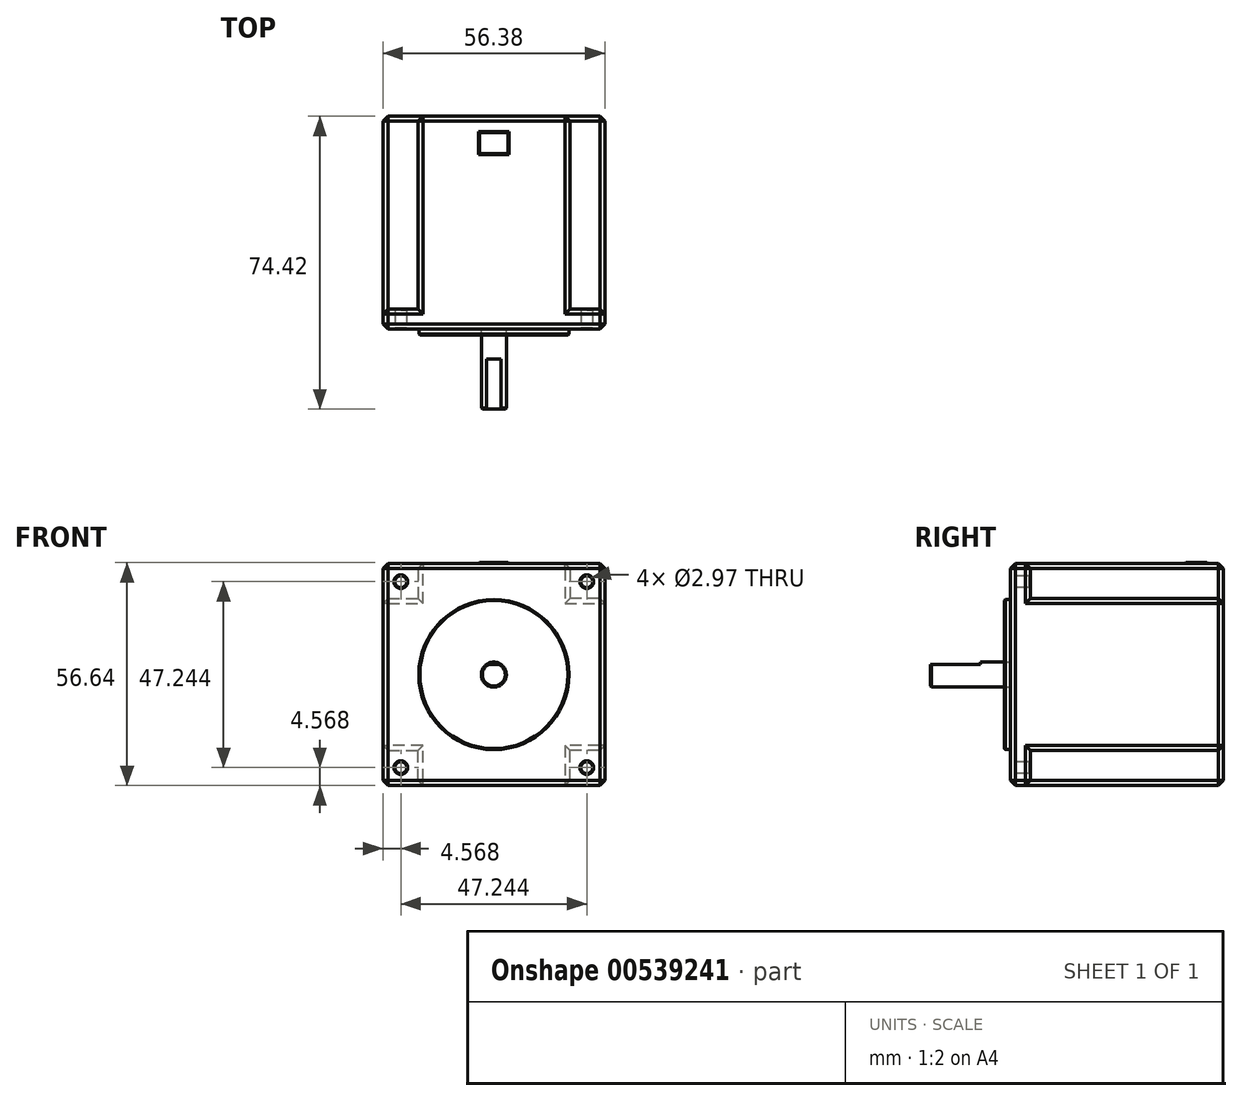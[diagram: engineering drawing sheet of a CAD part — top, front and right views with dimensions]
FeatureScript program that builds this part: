
annotation { "Feature Type Name" : "Feature", "Feature Type Description" : "" }
export const myFeature = defineFeature(function(context is Context, id is Id, definition is map)
    precondition{}
    {
        {
            var Q0;
            Q0=qCreatedBy(makeId("Front.planeOp"),FACE);
            var sketch = newSketch(context, id + "F0", { "sketchPlane" : qUnion([Q0])});
            skCircle(sketch, "E0", {"center": v(0, 0) * mm, "radius": 19.05 * mm});
            skLineSegment(sketch, "E1.bottom", {"start": v(28.2, 28.2) * mm, "end": v(-28.2, 28.2) * mm});
            skLineSegment(sketch, "E1.top", {"start": v(28.2, -28.2) * mm, "end": v(-28.2, -28.2) * mm});
            skLineSegment(sketch, "E1.left", {"start": v(28.2, 28.2) * mm, "end": v(28.2, -28.2) * mm});
            skLineSegment(sketch, "E1.right", {"start": v(-28.2, 28.2) * mm, "end": v(-28.2, -28.2) * mm});
            skCircle(sketch, "E2", {"center": v(0, 0) * mm, "radius": 3.18 * mm});
            skCircle(sketch, "E3", {"center": v(-23.62, 23.62) * mm, "radius": 1.49 * mm});
            skCircle(sketch, "E4", {"center": v(23.62, 23.62) * mm, "radius": 1.49 * mm});
            skCircle(sketch, "E5", {"center": v(23.62, -23.62) * mm, "radius": 1.49 * mm});
            skCircle(sketch, "E6", {"center": v(-23.62, -23.62) * mm, "radius": 1.49 * mm});
            skLineSegment(sketch, "E7", {"start": v(-23.62, 23.62) * mm, "end": v(-23.62, 28.2) * mm, "construction": true});
            skLineSegment(sketch, "E8", {"start": v(-23.62, 28.2) * mm, "end": v(-23.62, 23.62) * mm, "construction": true});
            skLineSegment(sketch, "E9", {"start": v(-23.62, 23.62) * mm, "end": v(-28.2, 23.62) * mm, "construction": true});
            skLineSegment(sketch, "E10", {"start": v(23.62, 23.62) * mm, "end": v(23.62, 28.2) * mm, "construction": true});
            skLineSegment(sketch, "E11", {"start": v(23.62, 23.62) * mm, "end": v(28.2, 23.62) * mm, "construction": true});
            skLineSegment(sketch, "E12", {"start": v(23.62, -23.62) * mm, "end": v(28.2, -23.62) * mm, "construction": true});
            skLineSegment(sketch, "E13", {"start": v(23.62, -23.62) * mm, "end": v(23.62, -28.2) * mm, "construction": true});
            skLineSegment(sketch, "E14", {"start": v(-23.62, -23.62) * mm, "end": v(-23.62, -28.2) * mm, "construction": true});
            skLineSegment(sketch, "E15", {"start": v(-23.62, -23.62) * mm, "end": v(-28.2, -23.62) * mm, "construction": true});
            skSolve(sketch);
        }
        {
            var Q0;
            Q0=qSketchRegion(id+"F0",true);
            var Q1;
            Q1=makeQuery(id+"F0.imprint","IMPRINT",FACE,{"disambiguationData":[TD([[makeQuery(id+"F0.imprint","IMPRINT",EDGE,{"derivedFrom":sQuery(id+"F0.wireOp",EDGE,"E0")}),1.0]])]});
            var Q2;
            Q2=makeQuery(id+"F0.imprint","IMPRINT",FACE,{"disambiguationData":[TD([[makeQuery(id+"F0.imprint","IMPRINT",EDGE,{"derivedFrom":sQuery(id+"F0.wireOp",EDGE,"E2")}),1.0]])]});
            extrude(context, id + "F1", {"entities" : qUnion([Q0, Q1, Q2]), "oppositeDirection" : true, "depth" : 54.1 * mm});
        }
        {
            var Q0;
            Q0=makeQuery(id+"F0.imprint","IMPRINT",FACE,{"disambiguationData":[TD([[makeQuery(id+"F0.imprint","IMPRINT",EDGE,{"derivedFrom":sQuery(id+"F0.wireOp",EDGE,"E0")}),1.0]])]});
            extrude(context, id + "F2", {"entities" : qUnion([Q0]), "operationType" : NewBodyOperationType.ADD, "depth" : 1.52 * mm});
        }
        {
            var Q0;
            Q0=makeQuery(id+"F0.imprint","IMPRINT",FACE,{"disambiguationData":[TD([[makeQuery(id+"F0.imprint","IMPRINT",EDGE,{"derivedFrom":sQuery(id+"F0.wireOp",EDGE,"E2")}),1.0]])]});
            extrude(context, id + "F3", {"entities" : qUnion([Q0]), "depth" : 20.32 * mm});
        }
        {
            var Q0;
            Q0=makeQuery(id+"F3.opExtrude","CAP_FACE",FACE,{"disambiguationData":[OSD([sQuery(id+"F0.wireOp",EDGE,"E2")])],"isStart":false});
            var sketch = newSketch(context, id + "F4", { "sketchPlane" : qUnion([Q0])});
            skLineSegment(sketch, "E16", {"start": v(-1.8, 2.62) * mm, "end": v(1.8, 2.62) * mm});
            skSolve(sketch);
        }
        {
            var Q0;
            {var subQ0=sQuery(id+"F4.wireOp",EDGE,"E16");Q0=makeQuery(id+"F4.imprint","IMPRINT",FACE,{"disambiguationData":[TD([[makeQuery(id+"F4.imprint","IMPRINT",EDGE,{"derivedFrom":subQ0}),1.0]])]});}
            extrude(context, id + "F5", {"entities" : qUnion([Q0]), "operationType" : NewBodyOperationType.REMOVE, "oppositeDirection" : true, "depth" : 12.7 * mm});
        }
        {
            var Q0;
            Q0=makeQuery(id+"F1.opExtrude","CAP_FACE",FACE,{"disambiguationData":[OSD([sQuery(id+"F0.wireOp",EDGE,"E1.bottom"),sQuery(id+"F0.wireOp",EDGE,"E1.top"),sQuery(id+"F0.wireOp",EDGE,"E1.left"),sQuery(id+"F0.wireOp",EDGE,"E1.right"),sQuery(id+"F0.wireOp",EDGE,"E3"),sQuery(id+"F0.wireOp",EDGE,"E4"),sQuery(id+"F0.wireOp",EDGE,"E5"),sQuery(id+"F0.wireOp",EDGE,"E6")])],"isStart":false});
            var sketch = newSketch(context, id + "F6", { "sketchPlane" : qUnion([Q0])});
            skLineSegment(sketch, "E17.bottom", {"start": v(-28.2, 28.2) * mm, "end": v(-19.3, 28.2) * mm});
            skLineSegment(sketch, "E17.top", {"start": v(-28.2, 19.3) * mm, "end": v(-19.3, 19.3) * mm});
            skLineSegment(sketch, "E17.left", {"start": v(-28.2, 28.2) * mm, "end": v(-28.2, 19.3) * mm});
            skLineSegment(sketch, "E17.right", {"start": v(-19.3, 28.2) * mm, "end": v(-19.3, 19.3) * mm});
            skLineSegment(sketch, "E18.bottom", {"start": v(28.2, 28.2) * mm, "end": v(19.3, 28.2) * mm});
            skLineSegment(sketch, "E18.top", {"start": v(28.2, 19.3) * mm, "end": v(19.3, 19.3) * mm});
            skLineSegment(sketch, "E18.left", {"start": v(28.2, 28.2) * mm, "end": v(28.2, 19.3) * mm});
            skLineSegment(sketch, "E18.right", {"start": v(19.3, 28.2) * mm, "end": v(19.3, 19.3) * mm});
            skLineSegment(sketch, "E19.bottom", {"start": v(28.2, -28.2) * mm, "end": v(19.3, -28.2) * mm});
            skLineSegment(sketch, "E19.top", {"start": v(28.2, -19.3) * mm, "end": v(19.3, -19.3) * mm});
            skLineSegment(sketch, "E19.left", {"start": v(28.2, -28.2) * mm, "end": v(28.2, -19.3) * mm});
            skLineSegment(sketch, "E19.right", {"start": v(19.3, -28.2) * mm, "end": v(19.3, -19.3) * mm});
            skLineSegment(sketch, "E20.bottom", {"start": v(-28.2, -28.2) * mm, "end": v(-19.3, -28.2) * mm});
            skLineSegment(sketch, "E20.top", {"start": v(-28.2, -19.3) * mm, "end": v(-19.3, -19.3) * mm});
            skLineSegment(sketch, "E20.left", {"start": v(-28.2, -28.2) * mm, "end": v(-28.2, -19.3) * mm});
            skLineSegment(sketch, "E20.right", {"start": v(-19.3, -28.2) * mm, "end": v(-19.3, -19.3) * mm});
            skSolve(sketch);
        }
        {
            var Q0;
            Q0=qSketchRegion(id+"F6",true);
            var Q1;
            {var subQ0=sQuery(id+"F0.wireOp",EDGE,"E1.right");var subQ1=sQuery(id+"F0.wireOp",EDGE,"E1.left");var subQ2=sQuery(id+"F0.wireOp",EDGE,"E1.top");var subQ3=sQuery(id+"F0.wireOp",EDGE,"E1.bottom");var subQ4=sQuery(id+"F0.wireOp",EDGE,"E3");var subQ5=sQuery(id+"F0.wireOp",EDGE,"E4");var subQ6=sQuery(id+"F0.wireOp",EDGE,"E5");var subQ7=sQuery(id+"F0.wireOp",EDGE,"E6");Q1=makeQuery(id+"F2.boolean.opBoolean","SPLIT",FACE,{"disambiguationData":[TD([makeQuery(id+"F1.opExtrude","SWEPT_FACE",FACE,{"disambiguationData":[OSD([subQ3])]})])],"derivedFrom":makeQuery(id+"F1.opExtrude","CAP_FACE",FACE,{"disambiguationData":[OSD([subQ3,subQ2,subQ1,subQ0,subQ4,subQ5,subQ6,subQ7])],"isStart":true})});}
            extrude(context, id + "F7", {"entities" : qUnion([Q0]), "operationType" : NewBodyOperationType.REMOVE, "oppositeDirection" : true, "endBoundEntityFace" : qUnion([Q1]), "depth" : 49.02 * mm});
        }
        {
            var Q0;
            Q0=makeQuery(id+"F1.opExtrude","SWEPT_FACE",FACE,{"disambiguationData":[OSD([sQuery(id+"F0.wireOp",EDGE,"E1.right")])]});
            var Q1;
            Q1=makeQuery(id+"F1.opExtrude","SWEPT_FACE",FACE,{"disambiguationData":[OSD([sQuery(id+"F0.wireOp",EDGE,"E1.bottom")])]});
            var Q2;
            Q2=makeQuery(id+"F1.opExtrude","SWEPT_FACE",FACE,{"disambiguationData":[OSD([sQuery(id+"F0.wireOp",EDGE,"E1.left")])]});
            var Q3;
            Q3=makeQuery(id+"F1.opExtrude","SWEPT_FACE",FACE,{"disambiguationData":[OSD([sQuery(id+"F0.wireOp",EDGE,"E1.top")])]});
            var Q4;
            Q4=makeQuery(id+"F1.opExtrude","CAP_FACE",FACE,{"disambiguationData":[OSD([sQuery(id+"F0.wireOp",EDGE,"E1.bottom"),sQuery(id+"F0.wireOp",EDGE,"E1.top"),sQuery(id+"F0.wireOp",EDGE,"E1.left"),sQuery(id+"F0.wireOp",EDGE,"E1.right"),sQuery(id+"F0.wireOp",EDGE,"E3"),sQuery(id+"F0.wireOp",EDGE,"E4"),sQuery(id+"F0.wireOp",EDGE,"E5"),sQuery(id+"F0.wireOp",EDGE,"E6")])],"isStart":false});
            chamfer(context, id + "F8", {"entities" : qUnion([Q0, Q1, Q2, Q3, Q4]), "width" : 1.27 * mm, "tangentPropagation" : true});
        }
        {
            var Q0;
            Q0=makeQuery(id+"F7.boolean.opBoolean","INTERSECT",EDGE,{"derivedFrom":[makeQuery(id+"F1.opExtrude","SWEPT_FACE",FACE,{"disambiguationData":[OSD([sQuery(id+"F0.wireOp",EDGE,"E3")])]}),makeQuery(id+"F7.opExtrude","CAP_FACE",FACE,{"disambiguationData":[OSD([sQuery(id+"F6.wireOp",EDGE,"E18.bottom"),sQuery(id+"F6.wireOp",EDGE,"E18.top"),sQuery(id+"F6.wireOp",EDGE,"E18.left"),sQuery(id+"F6.wireOp",EDGE,"E18.right")])],"isStart":false})]});
            var Q1;
            Q1=makeQuery(id+"F7.boolean.opBoolean","INTERSECT",EDGE,{"derivedFrom":[makeQuery(id+"F1.opExtrude","SWEPT_FACE",FACE,{"disambiguationData":[OSD([sQuery(id+"F0.wireOp",EDGE,"E6")])]}),makeQuery(id+"F7.opExtrude","CAP_FACE",FACE,{"disambiguationData":[OSD([sQuery(id+"F6.wireOp",EDGE,"E19.bottom"),sQuery(id+"F6.wireOp",EDGE,"E19.top"),sQuery(id+"F6.wireOp",EDGE,"E19.left"),sQuery(id+"F6.wireOp",EDGE,"E19.right")])],"isStart":false})]});
            var Q2;
            Q2=makeQuery(id+"F7.boolean.opBoolean","INTERSECT",EDGE,{"derivedFrom":[makeQuery(id+"F1.opExtrude","SWEPT_FACE",FACE,{"disambiguationData":[OSD([sQuery(id+"F0.wireOp",EDGE,"E4")])]}),makeQuery(id+"F7.opExtrude","CAP_FACE",FACE,{"disambiguationData":[OSD([sQuery(id+"F6.wireOp",EDGE,"E17.bottom"),sQuery(id+"F6.wireOp",EDGE,"E17.top"),sQuery(id+"F6.wireOp",EDGE,"E17.left"),sQuery(id+"F6.wireOp",EDGE,"E17.right")])],"isStart":false})]});
            var Q3;
            Q3=makeQuery(id+"F7.boolean.opBoolean","INTERSECT",EDGE,{"derivedFrom":[makeQuery(id+"F1.opExtrude","SWEPT_FACE",FACE,{"disambiguationData":[OSD([sQuery(id+"F0.wireOp",EDGE,"E5")])]}),makeQuery(id+"F7.opExtrude","CAP_FACE",FACE,{"disambiguationData":[OSD([sQuery(id+"F6.wireOp",EDGE,"E20.bottom"),sQuery(id+"F6.wireOp",EDGE,"E20.top"),sQuery(id+"F6.wireOp",EDGE,"E20.left"),sQuery(id+"F6.wireOp",EDGE,"E20.right")])],"isStart":false})]});
            var Q4;
            Q4=makeQuery(id+"F1.opExtrude","CAP_EDGE",EDGE,{"disambiguationData":[OSD([sQuery(id+"F0.wireOp",EDGE,"E5")])],"isStart":true});
            var Q5;
            Q5=makeQuery(id+"F1.opExtrude","CAP_EDGE",EDGE,{"disambiguationData":[OSD([sQuery(id+"F0.wireOp",EDGE,"E4")])],"isStart":true});
            var Q6;
            Q6=makeQuery(id+"F1.opExtrude","CAP_EDGE",EDGE,{"disambiguationData":[OSD([sQuery(id+"F0.wireOp",EDGE,"E3")])],"isStart":true});
            var Q7;
            Q7=makeQuery(id+"F1.opExtrude","CAP_EDGE",EDGE,{"disambiguationData":[OSD([sQuery(id+"F0.wireOp",EDGE,"E6")])],"isStart":true});
            var Q8;
            Q8=makeQuery(id+"F2.opExtrude","CAP_EDGE",EDGE,{"disambiguationData":[OSD([sQuery(id+"F0.wireOp",EDGE,"E0")])],"isStart":true});
            var Q9;
            Q9=makeQuery(id+"F2.opExtrude","CAP_EDGE",EDGE,{"disambiguationData":[OSD([sQuery(id+"F0.wireOp",EDGE,"E0")])],"isStart":false});
            var Q10;
            Q10=makeQuery(id+"F3.opExtrude","CAP_EDGE",EDGE,{"disambiguationData":[OSD([sQuery(id+"F0.wireOp",EDGE,"E2")])],"isStart":false});
            var Q11;
            Q11=makeQuery(id+"F5.boolean.opBoolean","COPY",EDGE,{"derivedFrom":makeQuery(id+"F5.opExtrude","CAP_EDGE",EDGE,{"disambiguationData":[OSD([sQuery(id+"F4.wireOp",EDGE,"E16")])],"isStart":true})});
            var Q12;
            Q12=makeQuery(id+"F2.opExtrude","CAP_EDGE",EDGE,{"disambiguationData":[OSD([sQuery(id+"F0.wireOp",EDGE,"E2")])],"isStart":false});
            chamfer(context, id + "F9", {"entities" : qUnion([Q0, Q1, Q2, Q3, Q4, Q5, Q6, Q7, Q8, Q9, Q10, Q11, Q12]), "width" : 0.25 * mm, "tangentPropagation" : true});
        }
        {
            var Q0;
            Q0=makeQuery(id+"F1.opExtrude","SWEPT_FACE",FACE,{"disambiguationData":[OSD([sQuery(id+"F0.wireOp",EDGE,"E1.bottom")])]});
            var sketch = newSketch(context, id + "F10", { "sketchPlane" : qUnion([Q0])});
            skLineSegment(sketch, "E21.bottom", {"start": v(2.6, 48.9) * mm, "end": v(-2.6, 48.9) * mm});
            skLineSegment(sketch, "E21.top", {"start": v(2.6, 45.63) * mm, "end": v(-2.6, 45.63) * mm});
            skLineSegment(sketch, "E21.left", {"start": v(2.6, 48.9) * mm, "end": v(2.6, 45.63) * mm});
            skLineSegment(sketch, "E21.right", {"start": v(-2.6, 48.9) * mm, "end": v(-2.6, 45.63) * mm});
            skPoint(sketch, "E21.middle", {"position": v(0, 47.26) * mm});
            skSolve(sketch);
        }
        {
            var Q0;
            Q0=qSketchRegion(id+"F10",true);
            extrude(context, id + "F11", {"entities" : qUnion([Q0]), "operationType" : NewBodyOperationType.ADD, "depth" : 0.25 * mm});
        }
    });
